# Revit family: Overhead_Door-CHI_Overhead_Doors-MaxSpeed
name_source: partatom
category: Specialty Equipment
units: mm (PartAtom-declared; Revit-internal decimal feet)

## family parameters
Always vertical = Yes
Classification Number = 23.30.10.21
Cut with Voids When Loaded = No
Enable Cutting in Views = No
Host = Wall
Maintain Annotation Orientation = No
Part Type = Normal
Room Calculation Point = No
Round Connector Dimension = Use Diameter
Shared = No

## types (4) — shared parameters
Apparent Load Phase 1 = 0 VA
Apparent Load Phase 2 = 0 VA
Apparent Load Phase 3 = 0 VA
Assembly Code = B2030410
Closing Speed = Up to 24 inches / second
Curtain Material = Rubber - C.H.I Overhead Doors - Reinforced Black Rubber
Description = Hight Speed Springless Impactable Rubber Door
Door Rail Depth = 6 "
Door Rail Width = 5 "
Keynote = 08 30 00
Load Classification = Motor
Manufacturer = C.H.I. Overhead Doors
Manufacturer Fax Number = 800-677-2650
Material = Metal - C.H.I Overhead Doors - Safety Yellow
Number of Poles = 3
Opening Speed = Up to 48 inches / second
Panel Thickness = 0.25 "
Power Factor = 1
Product Documentation Link = https://www.chiohd.com
Product Page URL = https://www.chiohd.com
Steel Gauge = 1/4"
URL = https://www.chiohd.com
Version = 2021-v1.a
Voltage = 0 V
Warranty URL = https://www.chiohd.com
zero-valued in all types: Default Elevation, Motor Cover Distance from Wall

## per-type parameters (varying)
| type | Axis Offset from Top | C Model | H Motor | Model | Motor Distance from Wall | Motor Distance to Shutterbox | Motor Length | Motor Side Offset | Motor Vertical Offset from Top | Shutter Box Depth | Shutter Box Height | V Motor |
| MaxSpeed - 350 - Safety Yellow - 1/4" Reinforced Rubber Curtain | 7.5 " | 1 | Yes | 350 | 26.88 " | 6.63 " | 19.38 " | 12 " | 32.66 " | 15 " | 15 " | No |
| MaxSpeed - 500 - Safety Yellow - 1/4" Reinforced Rubber Curtain | 9 " | 2 | No | 500 | 22.5 " | 8.75 " | 21.5 " | 14.13 " | 32.5 " | 20 " | 22 " | Yes |
| MaxSpeed - 1000 - Safety Yellow - 1/4" Reinforced Rubber Curtain | 10 " | 3 | No | 1000 | 23.63 " | 7.88 " | 22.5 " | 13.25 " | 32.5 " | 20 " | 20 " | Yes |
| MaxSpeed - 1200 - Safety Yellow - 1/4" Reinforced Rubber Curtain | 10 " | 4 | No | 1200 | 23.63 " | 7.88 " | 23.75 " | 13.25 " | 33.75 " | 24 " | 24 " | Yes |

## geometry (parser evidence)
native form markers: Sweep x26
no freeform markers — native parametric forms only
